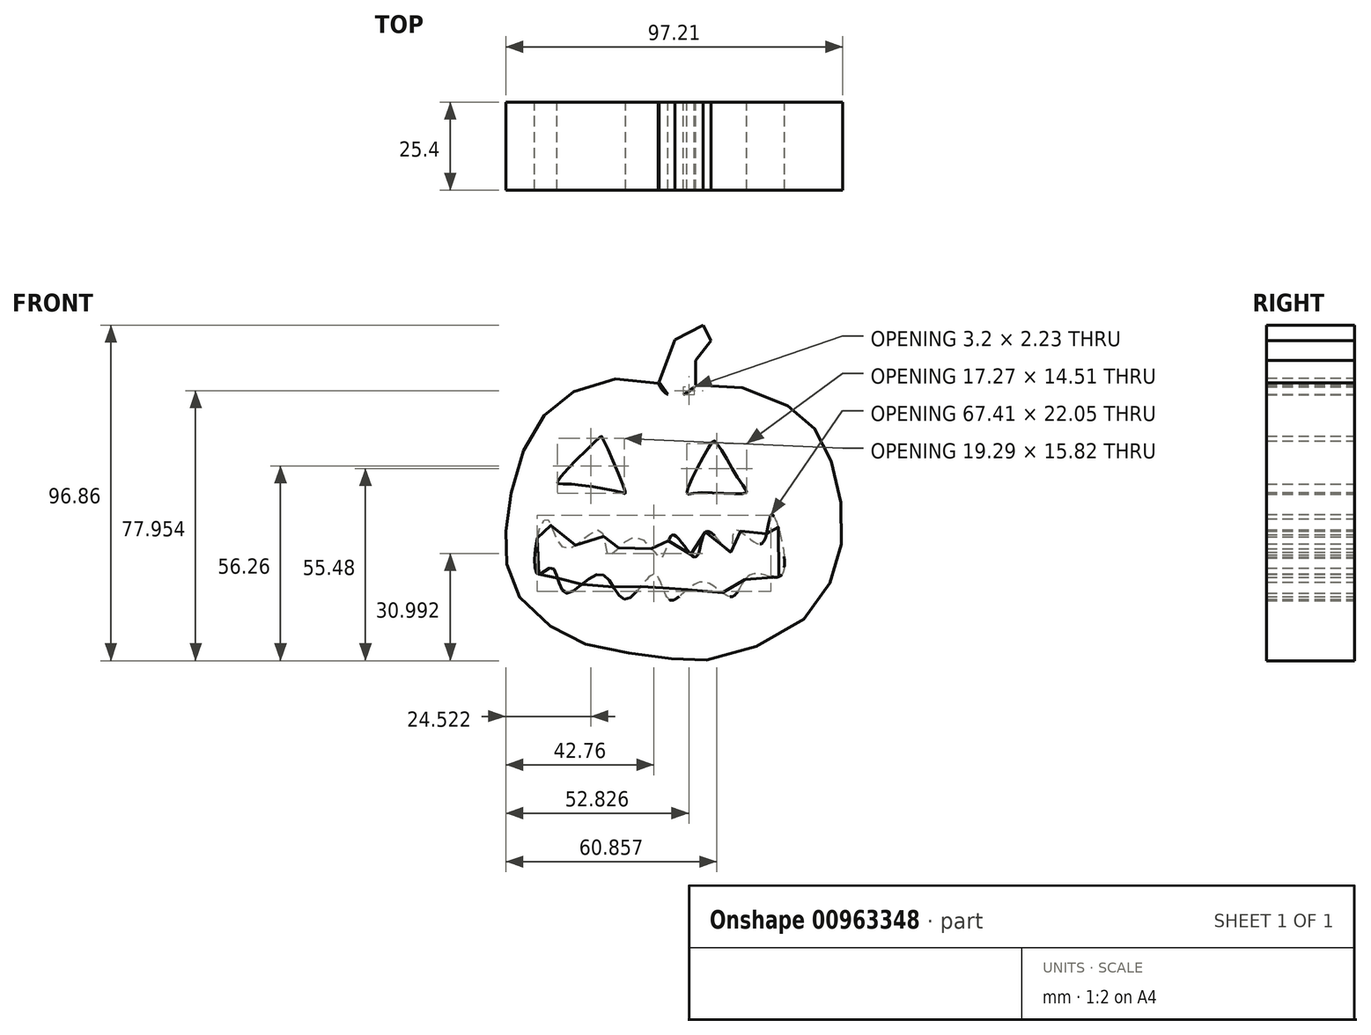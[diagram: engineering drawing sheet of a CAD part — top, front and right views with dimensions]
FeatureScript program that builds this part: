
annotation { "Feature Type Name" : "Feature", "Feature Type Description" : "" }
export const myFeature = defineFeature(function(context is Context, id is Id, definition is map)
    precondition{}
    {
        {
            var Q0;
            Q0=qCreatedBy(makeId("Front.planeOp"),FACE);
            var sketch = newSketch(context, id + "F0", { "sketchPlane" : qUnion([Q0])});
            skFitSpline(sketch, "E0", {"points": [v(-39.85, 26.7) * mm, v(-27.4, 39.75) * mm, v(-27, 39.75) * mm, v(-20.18, 23.5) * mm, v(-20.78, 23.5) * mm, v(-37.45, 26.1) * mm, v(-39.85, 26.7) * mm]});
            skFitSpline(sketch, "E1", {"points": [v(-2.5, 23.5) * mm, v(4.52, 37.75) * mm, v(5.72, 38.35) * mm, v(13.35, 26.1) * mm, v(14.56, 23.5) * mm, v(0, 23.5) * mm, v(-2.5, 23.5) * mm]});
            skFitSpline(sketch, "E2", {"points": [v(-45.68, 10.44) * mm, v(-42.67, 15.86) * mm, v(-37.45, 7.43) * mm, v(-27.6, 12.85) * mm, v(-25, 5.62) * mm, v(-17.17, 10.84) * mm, v(-9.74, 4.82) * mm, v(-6.53, 11.44) * mm, v(0, 5.02) * mm, v(3.31, 12.45) * mm, v(10.14, 6.42) * mm, v(11.54, 12.85) * mm, v(18.97, 8.83) * mm, v(21.99, 17.27) * mm, v(25, 0) * mm, v(16.16, 0) * mm, v(10.54, -6.42) * mm, v(1.7, -2.2) * mm, v(-7.33, -7.43) * mm, v(-11.75, 0) * mm, v(-20.18, -7.23) * mm, v(-27.2, 0) * mm, v(-37.45, -5.42) * mm, v(-41.26, 1.8) * mm, v(-45.28, 0) * mm, v(-45.68, 10.44) * mm]});
            skFitSpline(sketch, "E3", {"points": [v(-8.53, -24.1) * mm, v(3.31, -24.7) * mm, v(28.61, -15.06) * mm, v(39.85, 0) * mm, v(42.46, 15.26) * mm, v(39.25, 32.33) * mm, v(33.43, 43.17) * mm, v(21.99, 51) * mm, v(0, 54.61) * mm, v(-5.52, 51.4) * mm, v(-10.74, 55.21) * mm, v(-28.81, 55.21) * mm, v(-41.46, 48.19) * mm, v(-49.9, 35.14) * mm, v(-54.1, 18.07) * mm, v(-54.71, 6.83) * mm, v(-52.5, -3.82) * mm, v(-41.26, -15.46) * mm, v(-27.4, -21.29) * mm, v(-8.53, -24.1) * mm]});
            skFitSpline(sketch, "E4", {"points": [v(-10.74, 55.21) * mm, v(-8.53, 66.26) * mm, v(4.52, 65.86) * mm, v(2.71, 63.45) * mm, v(0, 57.23) * mm, v(0, 54.61) * mm, v(-5.52, 51.4) * mm, v(-10.74, 55.21) * mm]});
            skSolve(sketch);
        }
        {
            var Q0;
            Q0=makeQuery(id+"F0.imprint","IMPRINT",FACE,{"disambiguationData":[TD([[makeQuery(id+"F0.imprint","IMPRINT",EDGE,{"derivedFrom":sQuery(id+"F0.wireOp",EDGE,"E0")}),1.0]])]});
            extrude(context, id + "F1", {"entities" : qUnion([Q0]), "depth" : 25.4 * mm, "offsetDistance" : 25.4 * mm});
        }
        {
            var Q0;
            Q0=qCreatedBy(makeId("Front.planeOp"),FACE);
            var sketch = newSketch(context, id + "F2", { "sketchPlane" : qUnion([Q0])});
            skLineSegment(sketch, "E5", {"start": v(-10.52, 55.5) * mm, "end": v(-5.9, 67.75) * mm});
            skLineSegment(sketch, "E6", {"start": v(-5.9, 67.75) * mm, "end": v(2.2, 71.92) * mm});
            skLineSegment(sketch, "E7", {"start": v(2.2, 71.92) * mm, "end": v(4.47, 67.5) * mm});
            skLineSegment(sketch, "E8", {"start": v(4.47, 67.5) * mm, "end": v(0, 61.74) * mm});
            skLineSegment(sketch, "E9", {"start": v(0, 61.74) * mm, "end": v(0, 54.34) * mm});
            skLineSegment(sketch, "E10", {"start": v(0, 54.34) * mm, "end": v(-4.97, 50.87) * mm});
            skLineSegment(sketch, "E11", {"start": v(-4.97, 50.87) * mm, "end": v(-7.28, 50.87) * mm});
            skLineSegment(sketch, "E12", {"start": v(-7.28, 50.87) * mm, "end": v(-10.52, 55.5) * mm});
            skSolve(sketch);
        }
        {
            var Q0;
            Q0 = qSketchRegion(id + "F2", true);
            extrude(context, id + "F3", {"entities" : qUnion([Q0]), "operationType" : NewBodyOperationType.ADD, "depth" : 25.4 * mm, "offsetDistance" : 25.4 * mm});
        }
    });
